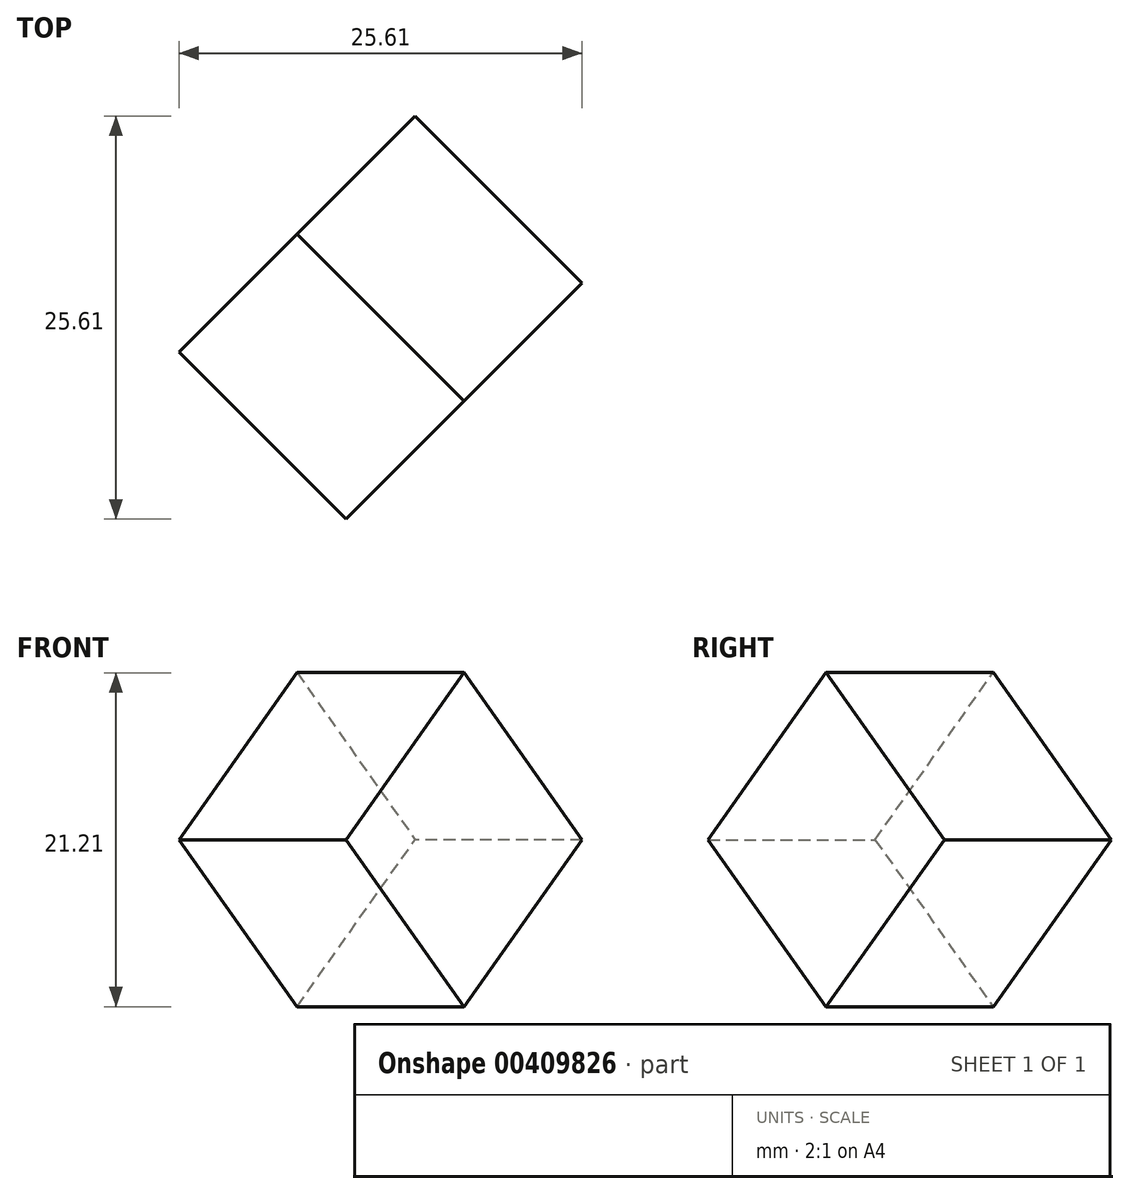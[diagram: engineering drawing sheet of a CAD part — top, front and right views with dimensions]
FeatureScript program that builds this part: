
annotation { "Feature Type Name" : "Feature", "Feature Type Description" : "" }
export const myFeature = defineFeature(function(context is Context, id is Id, definition is map)
    precondition{}
    {
        {
            var Q0;
            Q0=qCreatedBy(makeId("Front.planeOp"),FACE);
            var sketch = newSketch(context, id + "F0", { "sketchPlane" : qUnion([Q0])});
            skLineSegment(sketch, "E0.bottom", {"start": v(0, 0) * mm, "end": v(-15, 0) * mm});
            skLineSegment(sketch, "E0.top", {"start": v(0, 15) * mm, "end": v(-15, 15) * mm});
            skLineSegment(sketch, "E0.left", {"start": v(0, 0) * mm, "end": v(0, 15) * mm});
            skLineSegment(sketch, "E0.right", {"start": v(-15, 0) * mm, "end": v(-15, 15) * mm});
            skLineSegment(sketch, "E1", {"start": v(13.93, 0) * mm, "end": v(-37.55, 0) * mm, "construction": true});
            skLineSegment(sketch, "E2", {"start": v(0, 32.4) * mm, "end": v(0, -18.87) * mm, "construction": true});
            skSolve(sketch);
        }
        {
            var Q0;
            Q0=qSketchRegion(id+"F0",true);
            extrude(context, id + "F1", {"entities" : qUnion([Q0]), "depth" : 15 * mm});
        }
        {
            var Q0;
            Q0=qCreatedBy(makeId("Right.planeOp"),FACE);
            var sketch = newSketch(context, id + "F2", { "sketchPlane" : qUnion([Q0])});
            skLineSegment(sketch, "E3", {"start": v(0, 21.12) * mm, "end": v(0, -15.23) * mm, "construction": true});
            skSolve(sketch);
        }
        {
            var Q0;
            Q0=qCreatedBy(makeId("Top.planeOp"),FACE);
            var sketch = newSketch(context, id + "F3", { "sketchPlane" : qUnion([Q0])});
            skLineSegment(sketch, "E4", {"start": v(0, -24.85) * mm, "end": v(0, 18.43) * mm, "construction": true});
            skLineSegment(sketch, "E5", {"start": v(19.3, 0) * mm, "end": v(-30.7, 0) * mm, "construction": true});
            skSolve(sketch);
        }
        {
            var Q0;
            Q0=makeQuery(id+"F1.opExtrude","SWEPT_BODY",BODY,{"disambiguationData":[OSD([sQuery(id+"F0.wireOp",EDGE,"E0.bottom"),sQuery(id+"F0.wireOp",EDGE,"E0.top"),sQuery(id+"F0.wireOp",EDGE,"E0.left"),sQuery(id+"F0.wireOp",EDGE,"E0.right")])]});
            var Q1;
            Q1=sQuery(id+"F3.wireOp",EDGE,"E5");
            var Q2;
            Q2=sQuery(id+"F3.wireOp",EDGE,"E5");
            transform(context, id + "F4", {"entities" : qUnion([Q0]), "transformType" : TransformType.ROTATION, "transformAxis" : qUnion([Q2]), "angle" : 45 * degree, "makeCopy" : false});
        }
        {
            var Q0;
            Q0=makeQuery(id+"F1.opExtrude","SWEPT_BODY",BODY,{"disambiguationData":[OSD([sQuery(id+"F0.wireOp",EDGE,"E0.bottom"),sQuery(id+"F0.wireOp",EDGE,"E0.top"),sQuery(id+"F0.wireOp",EDGE,"E0.left"),sQuery(id+"F0.wireOp",EDGE,"E0.right")])]});
            var Q1;
            Q1=sQuery(id+"F2.wireOp",EDGE,"E3");
            transform(context, id + "F5", {"entities" : qUnion([Q0]), "transformType" : TransformType.ROTATION, "transformAxis" : qUnion([Q1]), "angle" : 45 * degree, "makeCopy" : false});
        }
    });
